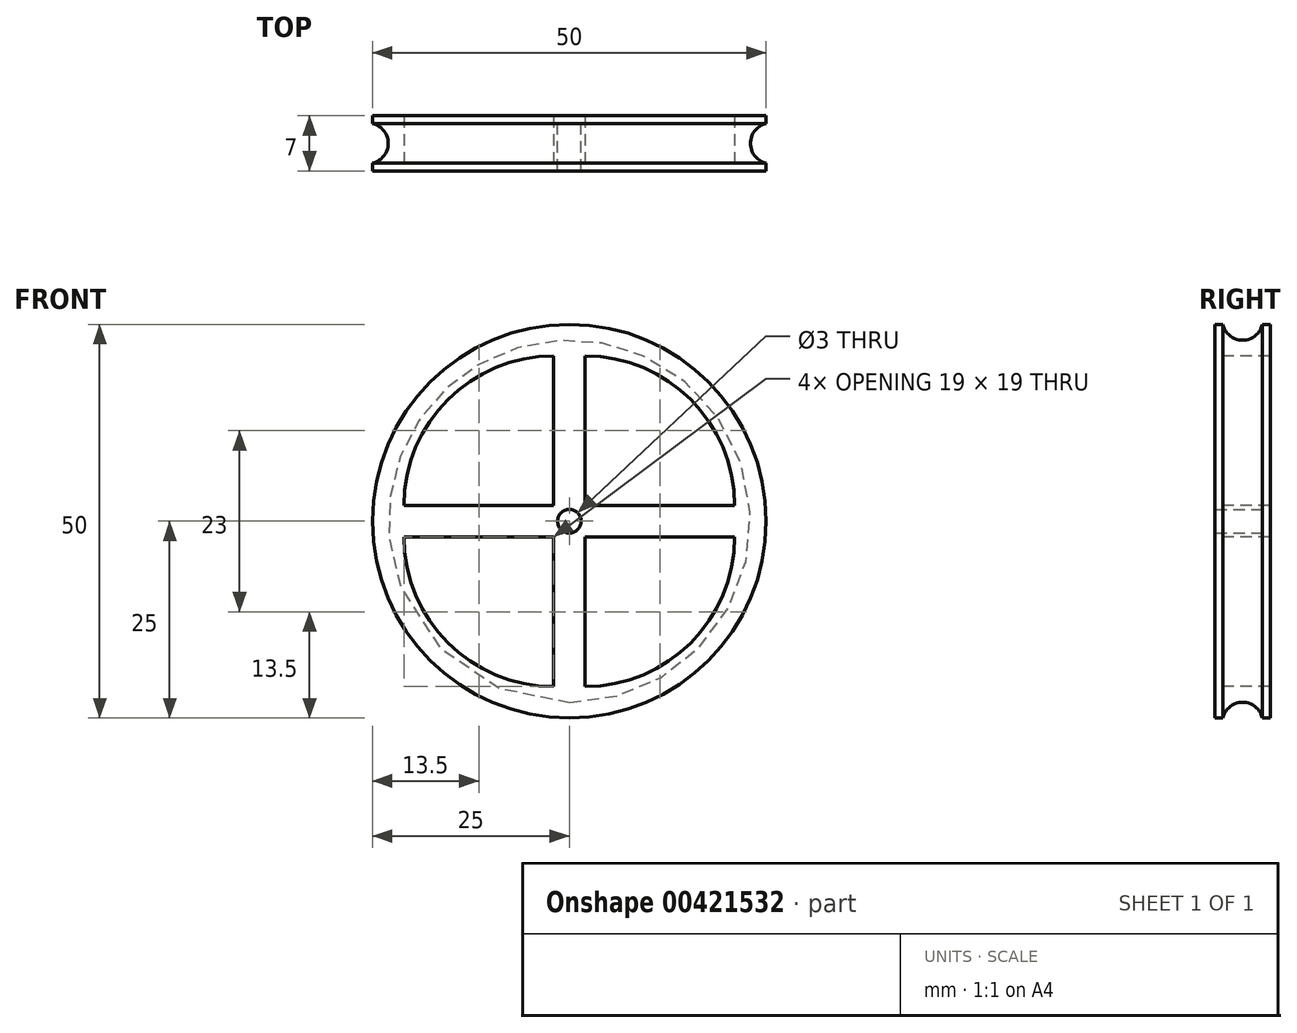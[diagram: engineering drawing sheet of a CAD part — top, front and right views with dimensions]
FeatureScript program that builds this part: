
annotation { "Feature Type Name" : "Feature", "Feature Type Description" : "" }
export const myFeature = defineFeature(function(context is Context, id is Id, definition is map)
    precondition{}
    {
        {
            var Q0;
            Q0=qCreatedBy(makeId("Front.planeOp"),FACE);
            var sketch = newSketch(context, id + "F0", { "sketchPlane" : qUnion([Q0])});
            skCircle(sketch, "E0", {"center": v(0, 0) * mm, "radius": 25 * mm});
            skSolve(sketch);
        }
        {
            var Q0;
            Q0 = qSketchRegion(id + "F0", true);
            extrude(context, id + "F1", {"entities" : qUnion([Q0]), "depth" : 7 * mm});
        }
        {
            var Q0;
            Q0=qCreatedBy(makeId("Right.planeOp"),FACE);
            var sketch = newSketch(context, id + "F2", { "sketchPlane" : qUnion([Q0])});
            skPoint(sketch, "E1.middle", {"position": v(-3.5, -7.5) * mm});
            skLineSegment(sketch, "E2.bottom", {"start": v(-7, 25) * mm, "end": v(0, 25) * mm, "construction": true});
            skLineSegment(sketch, "E2.top", {"start": v(-7, -25) * mm, "end": v(0, -25) * mm, "construction": true});
            skLineSegment(sketch, "E2.left", {"start": v(-7, 25) * mm, "end": v(-7, -25) * mm, "construction": true});
            skLineSegment(sketch, "E2.right", {"start": v(0, 25) * mm, "end": v(0, -25) * mm, "construction": true});
            skPoint(sketch, "E2.middle", {"position": v(-3.5, 0) * mm});
            skArc(sketch, "E3", {"start": v(-6, 25) * mm, "mid": v(-3.5, 23) * mm, "end": v(-1, 25) * mm});
            skPoint(sketch, "E3.centerSnap0", {"position": v(-3.5, 25) * mm});
            skLineSegment(sketch, "E4", {"start": v(-6, 25) * mm, "end": v(-1, 25) * mm});
            skSolve(sketch);
        }
        {
            var Q0;
            Q0=qCreatedBy(makeId("Right.planeOp"),FACE);
            var sketch = newSketch(context, id + "F3", { "sketchPlane" : qUnion([Q0])});
            skLineSegment(sketch, "E5", {"start": v(0, 0) * mm, "end": v(-16.35, 0) * mm});
            skSolve(sketch);
        }
        {
            var Q0;
            Q0 = qSketchRegion(id + "F2", true);
            var Q1;
            Q1=sQuery(id+"F3.wireOp",EDGE,"E5");
            revolve(context, id + "F4", {"operationType" : NewBodyOperationType.REMOVE, "entities" : qUnion([Q0]), "axis" : qUnion([Q1]), "revolveType" : RevolveType.FULL, "oppositeDirection" : true});
        }
        {
            var Q0;
            Q0=makeQuery(id+"F1.opExtrude","CAP_FACE",FACE,{"disambiguationData":[OSD([sQuery(id+"F0.wireOp",EDGE,"E0")])],"isStart":true});
            var sketch = newSketch(context, id + "F5", { "sketchPlane" : qUnion([Q0])});
            skCircle(sketch, "E6", {"center": v(0, 0) * mm, "radius": 1.5 * mm});
            skSolve(sketch);
        }
        {
            var Q0;
            Q0 = qSketchRegion(id + "F5", true);
            extrude(context, id + "F6", {"entities" : qUnion([Q0]), "operationType" : NewBodyOperationType.REMOVE, "endBound" : BoundingType.THROUGH_ALL, "oppositeDirection" : true, "depth" : 25 * mm});
        }
        {
            var Q0;
            Q0=makeQuery(id+"F1.opExtrude","CAP_FACE",FACE,{"disambiguationData":[OSD([sQuery(id+"F0.wireOp",EDGE,"E0")])],"isStart":false});
            var sketch = newSketch(context, id + "F7", { "sketchPlane" : qUnion([Q0])});
            skLineSegment(sketch, "E7", {"start": v(-2, 2) * mm, "end": v(-2, 21) * mm});
            skLineSegment(sketch, "E8", {"start": v(-2, 2) * mm, "end": v(-21, 2) * mm});
            skArc(sketch, "E9", {"start": v(-2, 21) * mm, "mid": v(-15.44, 15.44) * mm, "end": v(-21, 2) * mm});
            skLineSegment(sketch, "E10.MirrorCS", {"start": v(2, 2) * mm, "end": v(2, 21) * mm});
            skLineSegment(sketch, "E11.MirrorCS", {"start": v(2, 2) * mm, "end": v(21, 2) * mm});
            skArc(sketch, "E12.MirrorCS", {"start": v(2, 21) * mm, "mid": v(15.44, 15.44) * mm, "end": v(21, 2) * mm});
            skArc(sketch, "E13.MirrorCS", {"start": v(2, -21) * mm, "mid": v(15.44, -15.44) * mm, "end": v(21, -2) * mm});
            skLineSegment(sketch, "E14.MirrorCS", {"start": v(2, -2) * mm, "end": v(21, -2) * mm});
            skLineSegment(sketch, "E15.MirrorCS", {"start": v(2, -2) * mm, "end": v(2, -21) * mm});
            skArc(sketch, "E16.MirrorCS", {"start": v(-2, -21) * mm, "mid": v(-15.44, -15.44) * mm, "end": v(-21, -2) * mm});
            skLineSegment(sketch, "E17.MirrorCS", {"start": v(-2, -2) * mm, "end": v(-21, -2) * mm});
            skLineSegment(sketch, "E18.MirrorCS", {"start": v(-2, -2) * mm, "end": v(-2, -21) * mm});
            skSolve(sketch);
        }
        {
            var Q0;
            Q0 = qSketchRegion(id + "F7", true);
            extrude(context, id + "F8", {"entities" : qUnion([Q0]), "operationType" : NewBodyOperationType.REMOVE, "endBound" : BoundingType.THROUGH_ALL, "oppositeDirection" : true, "depth" : 25 * mm});
        }
    });
